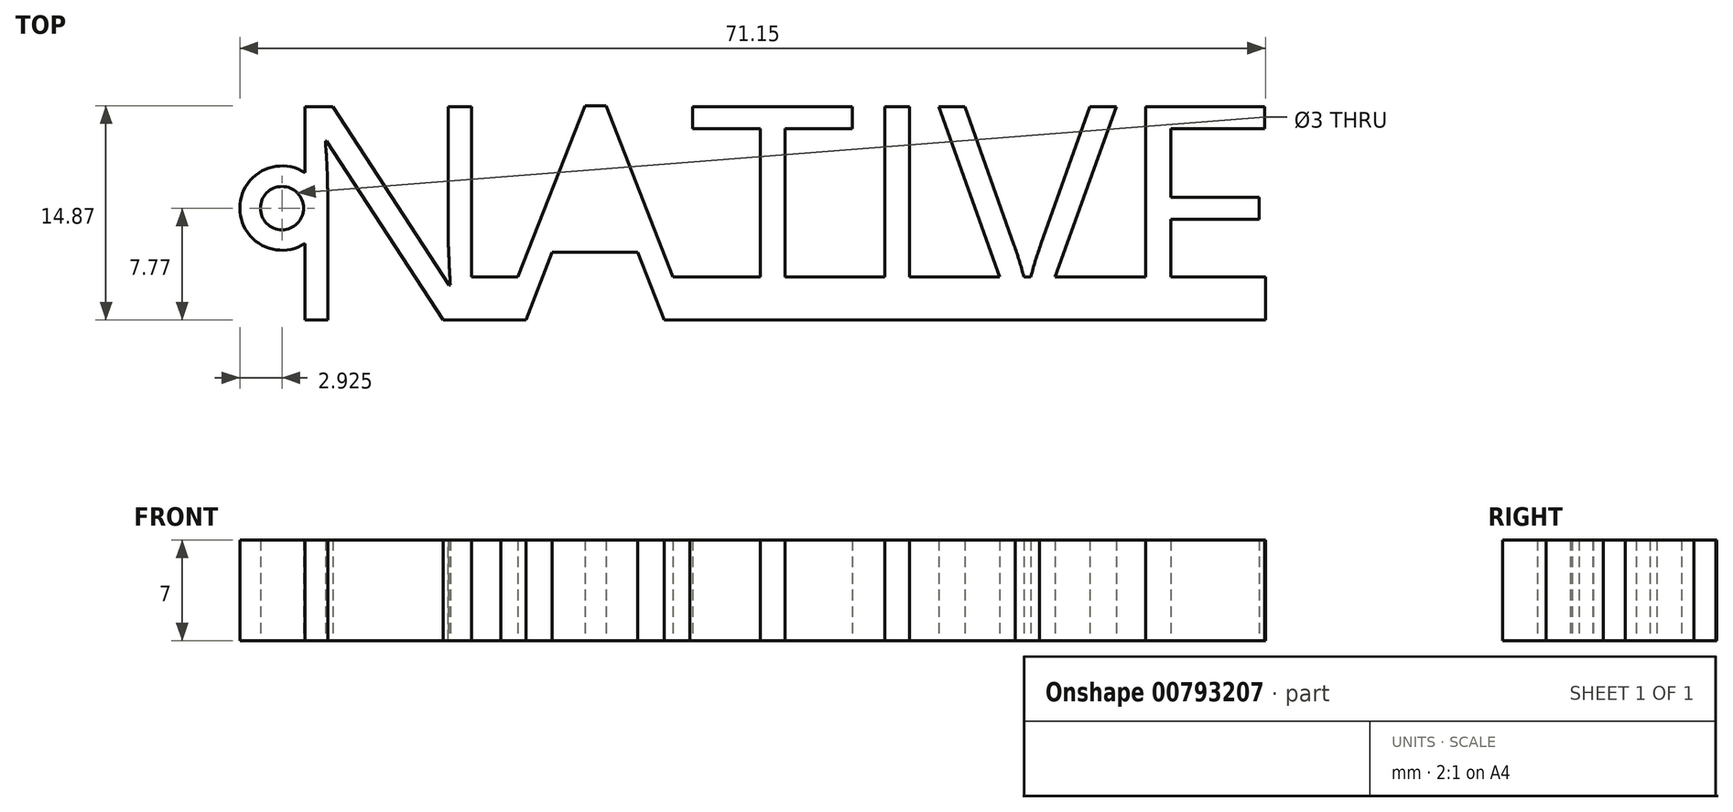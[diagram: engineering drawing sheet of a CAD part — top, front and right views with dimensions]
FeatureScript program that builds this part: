
annotation { "Feature Type Name" : "Feature", "Feature Type Description" : "" }
export const myFeature = defineFeature(function(context is Context, id is Id, definition is map)
    precondition{}
    {
        {
            var Q0;
            Q0=qCreatedBy(makeId("Top.planeOp"),FACE);
            var sketch = newSketch(context, id + "F0", { "sketchPlane" : qUnion([Q0])});
            skText(sketch, "E0", { "text": "NATIVE\n", "fontName": "OpenSans-Regular.ttf"});
            skLineSegment(sketch, "E1", {"start": v(-1.69, -5.3) * mm, "end": v(-4.82, -5.3) * mm});
            skLineSegment(sketch, "E2", {"start": v(-4.47, -8.3) * mm, "end": v(-2.22, -8.3) * mm});
            skLineSegment(sketch, "E3", {"start": v(42.43, -5.3) * mm, "end": v(42.43, -8.3) * mm});
            skLineSegment(sketch, "E4", {"start": v(42.43, -8.3) * mm, "end": v(25.88, -8.3) * mm});
            skLineSegment(sketch, "E5", {"start": v(-1.69, -5.3) * mm, "end": v(-0.66, -5.3) * mm});
            skCircle(sketch, "E6", {"center": v(-17.54, -0.53) * mm, "radius": 2.92 * mm});
            skCircle(sketch, "E7", {"center": v(-17.54, -0.53) * mm, "radius": 1.51 * mm});
            skLineSegment(sketch, "E8", {"start": v(9.26, -5.3) * mm, "end": v(42.94, -5.3) * mm});
            skLineSegment(sketch, "E9", {"start": v(42.94, -5.3) * mm, "end": v(42.94, -8.3) * mm});
            skLineSegment(sketch, "E10", {"start": v(42.94, -8.3) * mm, "end": v(9.73, -8.3) * mm});
            skLineSegment(sketch, "E11", {"start": v(9.73, -8.3) * mm, "end": v(9.26, -5.3) * mm});
            skLineSegment(sketch, "E12", {"start": v(41.77, -5.3) * mm, "end": v(50.68, -5.3) * mm});
            skLineSegment(sketch, "E13", {"start": v(50.68, -5.3) * mm, "end": v(50.68, -8.3) * mm});
            skLineSegment(sketch, "E14", {"start": v(50.68, -8.3) * mm, "end": v(42.94, -8.3) * mm});
            const initialGuessF0  = {"E0": [-0.018, -0.0083, 1, 0, 0.01493]};
            skSetInitialGuess(sketch, initialGuessF0);
            skSolve(sketch);
        }
        {
            var Q0;
            Q0 = qSketchRegion(id + "F0", true);
            var Q1;
            {var subQ0=sQuery(id+"F0.wireOp",EDGE,"E10");var subQ1=sQuery(id+"F0.wireOp",EDGE,"E0.sketch_text.stroke-21");var subQ2=makeQuery(id+"F0.imprint","INTERSECT",VERTEX,{"derivedFrom":[subQ1,subQ0]});Q1=makeQuery(id+"F0.imprint","IMPRINT",FACE,{"disambiguationData":[TD([[makeQuery(id+"F0.imprint","IMPRINT",EDGE,{"disambiguationData":[TD([[subQ2,1.0]])],"derivedFrom":subQ1}),1.0]])]});}
            var Q2;
            Q2=makeQuery(id+"F0.imprint","IMPRINT",FACE,{"disambiguationData":[TD([[makeQuery(id+"F0.imprint","IMPRINT",EDGE,{"derivedFrom":sQuery(id+"F0.wireOp",EDGE,"E0.sketch_text.stroke-49")}),-1.0]])]});
            var Q3;
            {var subQ0=sQuery(id+"F0.wireOp",EDGE,"E2");var subQ1=sQuery(id+"F0.wireOp",EDGE,"E0.sketch_text.stroke-14");var subQ2=makeQuery(id+"F0.imprint","INTERSECT",VERTEX,{"derivedFrom":[subQ1,subQ0]});Q3=makeQuery(id+"F0.imprint","IMPRINT",FACE,{"disambiguationData":[TD([[makeQuery(id+"F0.imprint","IMPRINT",EDGE,{"disambiguationData":[TD([[subQ2,1.0]])],"derivedFrom":subQ1}),1.0]])]});}
            var Q4;
            {var subQ0=sQuery(id+"F0.wireOp",EDGE,"E6");var subQ1=sQuery(id+"F0.wireOp",EDGE,"E0.sketch_text.stroke-6");var subQ2=makeQuery(id+"F0.imprint","INTERSECT",VERTEX,{"disambiguationData":[OD(0.0)],"derivedFrom":[subQ1,subQ0]});Q4=makeQuery(id+"F0.imprint","IMPRINT",FACE,{"disambiguationData":[TD([[makeQuery(id+"F0.imprint","IMPRINT",EDGE,{"disambiguationData":[TD([[subQ2,-1.0]])],"derivedFrom":subQ1}),-1.0]])]});}
            var Q5;
            {var subQ5=sQuery(id+"F0.wireOp",EDGE,"E0.sketch_text.stroke-41");var subQ8=sQuery(id+"F0.wireOp",EDGE,"E10");var subQ12=makeQuery(id+"F0.imprint","INTERSECT",VERTEX,{"derivedFrom":[subQ5,subQ8]});Q5=makeQuery(id+"F0.imprint","IMPRINT",FACE,{"disambiguationData":[TD([[makeQuery(id+"F0.imprint","IMPRINT",EDGE,{"disambiguationData":[TD([[subQ12,1.0]])],"derivedFrom":subQ5}),-1.0]])]});}
            var Q6;
            {var subQ0=sQuery(id+"F0.wireOp",EDGE,"E10");var subQ1=sQuery(id+"F0.wireOp",EDGE,"E0.sketch_text.stroke-38");var subQ2=makeQuery(id+"F0.imprint","INTERSECT",VERTEX,{"derivedFrom":[subQ1,subQ0]});Q6=makeQuery(id+"F0.imprint","IMPRINT",FACE,{"disambiguationData":[TD([[makeQuery(id+"F0.imprint","IMPRINT",EDGE,{"disambiguationData":[TD([[subQ2,1.0]])],"derivedFrom":subQ1}),1.0]])]});}
            var Q7;
            {var subQ0=sQuery(id+"F0.wireOp",EDGE,"E10");var subQ1=sQuery(id+"F0.wireOp",EDGE,"E0.sketch_text.stroke-41");var subQ2=makeQuery(id+"F0.imprint","INTERSECT",VERTEX,{"derivedFrom":[subQ1,subQ0]});Q7=makeQuery(id+"F0.imprint","IMPRINT",FACE,{"disambiguationData":[TD([[makeQuery(id+"F0.imprint","IMPRINT",EDGE,{"disambiguationData":[TD([[subQ2,1.0]])],"derivedFrom":subQ1}),1.0]])]});}
            var Q8;
            Q8=makeQuery(id+"F0.imprint","IMPRINT",FACE,{"disambiguationData":[TD([[makeQuery(id+"F0.imprint","IMPRINT",EDGE,{"derivedFrom":sQuery(id+"F0.wireOp",EDGE,"E7")}),1.0]])]});
            var Q9;
            Q9=makeQuery(id+"F0.imprint","IMPRINT",FACE,{"disambiguationData":[TD([[makeQuery(id+"F0.imprint","IMPRINT",EDGE,{"derivedFrom":sQuery(id+"F0.wireOp",EDGE,"E7")}),-1.0]])]});
            var Q10;
            {var subQ6=sQuery(id+"F0.wireOp",EDGE,"E0.sketch_text.stroke-44");Q10=makeQuery(id+"F0.imprint","IMPRINT",FACE,{"disambiguationData":[TD([[makeQuery(id+"F0.imprint","IMPRINT",EDGE,{"derivedFrom":subQ6}),-1.0]])]});}
            var Q11;
            {var subQ0=sQuery(id+"F0.wireOp",EDGE,"E0.sketch_text.stroke-37");Q11=makeQuery(id+"F0.imprint","IMPRINT",FACE,{"disambiguationData":[TD([[makeQuery(id+"F0.imprint","IMPRINT",EDGE,{"derivedFrom":subQ0}),-1.0]])]});}
            var Q12;
            {var subQ0=sQuery(id+"F0.wireOp",EDGE,"E3");Q12=makeQuery(id+"F0.imprint","IMPRINT",FACE,{"disambiguationData":[TD([[makeQuery(id+"F0.imprint","IMPRINT",EDGE,{"derivedFrom":subQ0}),1.0]])]});}
            var Q13;
            {var subQ0=sQuery(id+"F0.wireOp",EDGE,"E10");var subQ1=sQuery(id+"F0.wireOp",EDGE,"E0.sketch_text.stroke-36");var subQ2=makeQuery(id+"F0.imprint","INTERSECT",VERTEX,{"derivedFrom":[subQ1,subQ0]});Q13=makeQuery(id+"F0.imprint","IMPRINT",FACE,{"disambiguationData":[TD([[makeQuery(id+"F0.imprint","IMPRINT",EDGE,{"disambiguationData":[TD([[subQ2,-1.0]])],"derivedFrom":subQ1}),-1.0]])]});}
            var Q14;
            {var subQ1=sQuery(id+"F0.wireOp",EDGE,"E0.sketch_text.stroke-40");Q14=makeQuery(id+"F0.imprint","IMPRINT",FACE,{"disambiguationData":[TD([[makeQuery(id+"F0.imprint","IMPRINT",EDGE,{"derivedFrom":subQ1}),-1.0]])]});}
            var Q15;
            Q15=makeQuery(id+"F0.imprint","IMPRINT",FACE,{"disambiguationData":[TD([[makeQuery(id+"F0.imprint","IMPRINT",EDGE,{"derivedFrom":sQuery(id+"F0.wireOp",EDGE,"E0.sketch_text.stroke-23")}),1.0]])]});
            var Q16;
            {var subQ0=sQuery(id+"F0.wireOp",EDGE,"E10");var subQ1=sQuery(id+"F0.wireOp",EDGE,"E0.sketch_text.stroke-35");var subQ2=makeQuery(id+"F0.imprint","INTERSECT",VERTEX,{"derivedFrom":[subQ1,subQ0]});Q16=makeQuery(id+"F0.imprint","IMPRINT",FACE,{"disambiguationData":[TD([[makeQuery(id+"F0.imprint","IMPRINT",EDGE,{"disambiguationData":[TD([[subQ2,1.0]])],"derivedFrom":subQ1}),1.0]])]});}
            var Q17;
            {var subQ5=sQuery(id+"F0.wireOp",EDGE,"E11");Q17=makeQuery(id+"F0.imprint","IMPRINT",FACE,{"disambiguationData":[TD([[makeQuery(id+"F0.imprint","IMPRINT",EDGE,{"derivedFrom":subQ5}),-1.0]])]});}
            var Q18;
            {var subQ0=sQuery(id+"F0.wireOp",EDGE,"E0.sketch_text.stroke-30");Q18=makeQuery(id+"F0.imprint","IMPRINT",FACE,{"disambiguationData":[TD([[makeQuery(id+"F0.imprint","IMPRINT",EDGE,{"derivedFrom":subQ0}),-1.0]])]});}
            var Q19;
            {var subQ7=sQuery(id+"F0.wireOp",EDGE,"E0.sketch_text.stroke-0");Q19=makeQuery(id+"F0.imprint","IMPRINT",FACE,{"disambiguationData":[TD([[makeQuery(id+"F0.imprint","IMPRINT",EDGE,{"derivedFrom":subQ7}),-1.0]])]});}
            var Q20;
            Q20=makeQuery(id+"F0.imprint","IMPRINT",FACE,{"disambiguationData":[TD([[makeQuery(id+"F0.imprint","IMPRINT",EDGE,{"derivedFrom":sQuery(id+"F0.wireOp",EDGE,"E0.sketch_text.stroke-15")}),-1.0]])]});
            var Q21;
            {var subQ0=sQuery(id+"F0.wireOp",EDGE,"E10");var subQ1=sQuery(id+"F0.wireOp",EDGE,"E0.sketch_text.stroke-29");var subQ2=makeQuery(id+"F0.imprint","INTERSECT",VERTEX,{"derivedFrom":[subQ1,subQ0]});Q21=makeQuery(id+"F0.imprint","IMPRINT",FACE,{"disambiguationData":[TD([[makeQuery(id+"F0.imprint","IMPRINT",EDGE,{"disambiguationData":[TD([[subQ2,-1.0]])],"derivedFrom":subQ1}),-1.0]])]});}
            var Q22;
            {var subQ0=sQuery(id+"F0.wireOp",EDGE,"E0.sketch_text.stroke-47");var subQ1=sQuery(id+"F0.wireOp",EDGE,"E0.sketch_text.stroke-46");var subQ2=makeQuery(id+"F0.imprint","INTERSECT",VERTEX,{"derivedFrom":[subQ1,subQ0]});Q22=makeQuery(id+"F0.imprint","IMPRINT",FACE,{"disambiguationData":[TD([[makeQuery(id+"F0.imprint","IMPRINT",EDGE,{"disambiguationData":[TD([[subQ2,1.0]])],"derivedFrom":subQ1}),1.0]])]});}
            var Q23;
            {var subQ5=sQuery(id+"F0.wireOp",EDGE,"E3");Q23=makeQuery(id+"F0.imprint","IMPRINT",FACE,{"disambiguationData":[TD([[makeQuery(id+"F0.imprint","IMPRINT",EDGE,{"derivedFrom":subQ5}),-1.0]])]});}
            extrude(context, id + "F1", {"entities" : qUnion([Q0, Q1, Q2, Q3, Q4, Q5, Q6, Q7, Q8, Q9, Q10, Q11, Q12, Q13, Q14, Q15, Q16, Q17, Q18, Q19, Q20, Q21, Q22, Q23]), "depth" : 7 * mm, "offsetDistance" : 25 * mm});
        }
        {
            var Q0;
            Q0=sQuery(id+"F0.wireOp",VERTEX,"E6.center");
            var Q1;
            Q1=makeQuery(id+"F1.opExtrude","SWEPT_BODY",BODY,{"disambiguationData":[OSD([sQuery(id+"F0.wireOp",EDGE,"E0.sketch_text.stroke-0"),sQuery(id+"F0.wireOp",EDGE,"E0.sketch_text.stroke-1"),sQuery(id+"F0.wireOp",EDGE,"E0.sketch_text.stroke-2"),sQuery(id+"F0.wireOp",EDGE,"E0.sketch_text.stroke-3"),sQuery(id+"F0.wireOp",EDGE,"E0.sketch_text.stroke-4"),sQuery(id+"F0.wireOp",EDGE,"E0.sketch_text.stroke-5"),sQuery(id+"F0.wireOp",EDGE,"E0.sketch_text.stroke-6"),sQuery(id+"F0.wireOp",EDGE,"E0.sketch_text.stroke-7"),sQuery(id+"F0.wireOp",EDGE,"E0.sketch_text.stroke-8"),sQuery(id+"F0.wireOp",EDGE,"E0.sketch_text.stroke-9"),sQuery(id+"F0.wireOp",EDGE,"E0.sketch_text.stroke-10"),sQuery(id+"F0.wireOp",EDGE,"E0.sketch_text.stroke-11"),sQuery(id+"F0.wireOp",EDGE,"E0.sketch_text.stroke-12"),sQuery(id+"F0.wireOp",EDGE,"E0.sketch_text.stroke-13"),sQuery(id+"F0.wireOp",EDGE,"E0.sketch_text.stroke-14"),sQuery(id+"F0.wireOp",EDGE,"E0.sketch_text.stroke-15"),sQuery(id+"F0.wireOp",EDGE,"E0.sketch_text.stroke-16"),sQuery(id+"F0.wireOp",EDGE,"E0.sketch_text.stroke-17"),sQuery(id+"F0.wireOp",EDGE,"E0.sketch_text.stroke-18"),sQuery(id+"F0.wireOp",EDGE,"E0.sketch_text.stroke-19"),sQuery(id+"F0.wireOp",EDGE,"E0.sketch_text.stroke-20"),sQuery(id+"F0.wireOp",EDGE,"E0.sketch_text.stroke-21"),sQuery(id+"F0.wireOp",EDGE,"E0.sketch_text.stroke-22"),sQuery(id+"F0.wireOp",EDGE,"E0.sketch_text.stroke-29"),sQuery(id+"F0.wireOp",EDGE,"E0.sketch_text.stroke-30"),sQuery(id+"F0.wireOp",EDGE,"E0.sketch_text.stroke-31"),sQuery(id+"F0.wireOp",EDGE,"E0.sketch_text.stroke-32"),sQuery(id+"F0.wireOp",EDGE,"E0.sketch_text.stroke-33"),sQuery(id+"F0.wireOp",EDGE,"E0.sketch_text.stroke-34"),sQuery(id+"F0.wireOp",EDGE,"E0.sketch_text.stroke-35"),sQuery(id+"F0.wireOp",EDGE,"E0.sketch_text.stroke-36"),sQuery(id+"F0.wireOp",EDGE,"E0.sketch_text.stroke-37"),sQuery(id+"F0.wireOp",EDGE,"E0.sketch_text.stroke-38"),sQuery(id+"F0.wireOp",EDGE,"E0.sketch_text.stroke-40"),sQuery(id+"F0.wireOp",EDGE,"E0.sketch_text.stroke-41"),sQuery(id+"F0.wireOp",EDGE,"E0.sketch_text.stroke-43"),sQuery(id+"F0.wireOp",EDGE,"E0.sketch_text.stroke-44"),sQuery(id+"F0.wireOp",EDGE,"E0.sketch_text.stroke-45"),sQuery(id+"F0.wireOp",EDGE,"E0.sketch_text.stroke-46"),sQuery(id+"F0.wireOp",EDGE,"E0.sketch_text.stroke-47"),sQuery(id+"F0.wireOp",EDGE,"E0.sketch_text.stroke-48"),sQuery(id+"F0.wireOp",EDGE,"E0.sketch_text.stroke-49"),sQuery(id+"F0.wireOp",EDGE,"E0.sketch_text.stroke-50"),sQuery(id+"F0.wireOp",EDGE,"E0.sketch_text.stroke-51"),sQuery(id+"F0.wireOp",EDGE,"E0.sketch_text.stroke-52"),sQuery(id+"F0.wireOp",EDGE,"E0.sketch_text.stroke-53"),sQuery(id+"F0.wireOp",EDGE,"E0.sketch_text.stroke-54"),sQuery(id+"F0.wireOp",EDGE,"E0.sketch_text.stroke-55"),sQuery(id+"F0.wireOp",EDGE,"E0.sketch_text.stroke-56"),sQuery(id+"F0.wireOp",EDGE,"E0.sketch_text.stroke-57"),sQuery(id+"F0.wireOp",EDGE,"E0.sketch_text.stroke-58"),sQuery(id+"F0.wireOp",EDGE,"E0.sketch_text.stroke-59"),sQuery(id+"F0.wireOp",EDGE,"E0.sketch_text.stroke-60"),sQuery(id+"F0.wireOp",EDGE,"E1"),sQuery(id+"F0.wireOp",EDGE,"E2"),sQuery(id+"F0.wireOp",EDGE,"E5"),sQuery(id+"F0.wireOp",EDGE,"E6"),sQuery(id+"F0.wireOp",EDGE,"E8"),sQuery(id+"F0.wireOp",EDGE,"E10")])]});
            hole(context, id + "F2", {"style" : HoleStyle.SIMPLE, "endStyle" : HoleEndStyle.THROUGH, "oppositeDirection" : true, "holeDiameter" : 3 * mm, "majorDiameter" : 5 * mm, "isTappedThrough" : true, "tappedDepth" : 12 * mm, "tapClearance" : 3, "locations" : qUnion([Q0]), "scope" : qUnion([Q1])});
        }
    });
